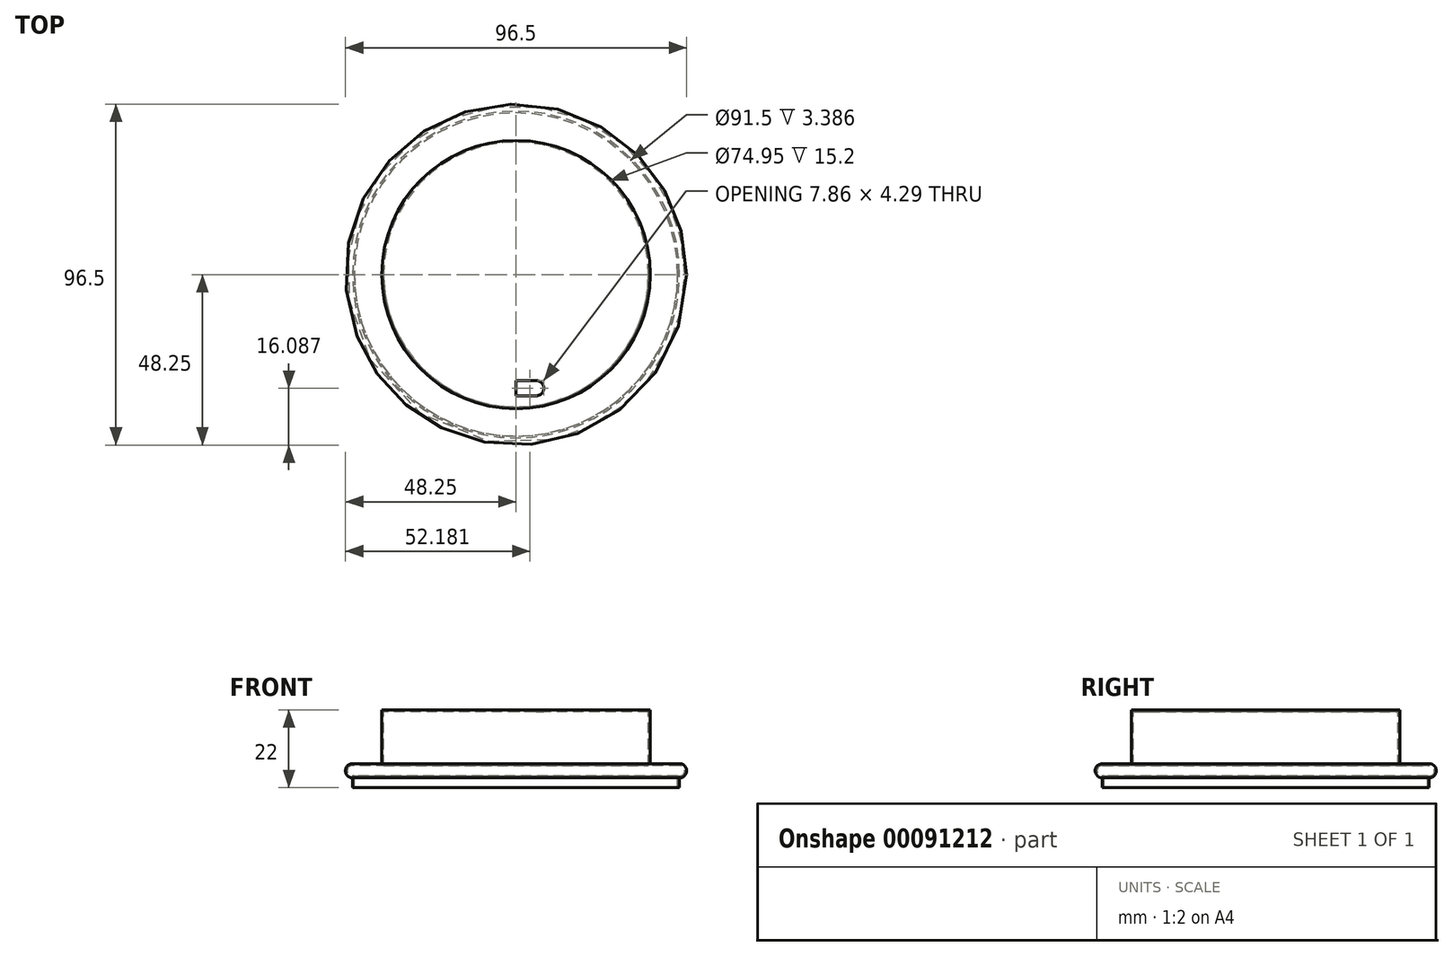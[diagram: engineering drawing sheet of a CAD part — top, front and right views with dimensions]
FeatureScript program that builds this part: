
annotation { "Feature Type Name" : "Feature", "Feature Type Description" : "" }
export const myFeature = defineFeature(function(context is Context, id is Id, definition is map)
    precondition{}
    {
        {
            var Q0;
            Q0=qCreatedBy(makeId("Front.planeOp"),FACE);
            var sketch = newSketch(context, id + "F0", { "sketchPlane" : qUnion([Q0])});
            skLineSegment(sketch, "E0.bottom", {"start": v(46.25, -3.4) * mm, "end": v(-46.25, -3.4) * mm});
            skLineSegment(sketch, "E0.top", {"start": v(46.25, 3.4) * mm, "end": v(-46.25, 3.4) * mm});
            skLineSegment(sketch, "E0.left", {"start": v(46.25, -3.4) * mm, "end": v(46.25, 3.4) * mm});
            skLineSegment(sketch, "E0.right", {"start": v(-46.25, -3.4) * mm, "end": v(-46.25, 3.4) * mm});
            skPoint(sketch, "E0.middle", {"position": v(0, 0) * mm});
            skLineSegment(sketch, "E1.bottom", {"start": v(-38.82, 12.6) * mm, "end": v(37.98, 12.6) * mm});
            skLineSegment(sketch, "E1.top", {"start": v(-38.82, 0) * mm, "end": v(37.98, 0) * mm});
            skLineSegment(sketch, "E1.left", {"start": v(-38.82, 12.6) * mm, "end": v(-38.82, 0) * mm});
            skLineSegment(sketch, "E1.right", {"start": v(37.98, 12.6) * mm, "end": v(37.98, 0) * mm});
            skLineSegment(sketch, "E2", {"start": v(0, 32.32) * mm, "end": v(0, -32.54) * mm});
            skLineSegment(sketch, "E3.bottom", {"start": v(-38.82, 18.6) * mm, "end": v(37.98, 18.6) * mm});
            skLineSegment(sketch, "E3.left", {"start": v(-38.82, 18.6) * mm, "end": v(-38.82, 12.6) * mm});
            skLineSegment(sketch, "E3.right", {"start": v(37.98, 18.6) * mm, "end": v(37.98, 12.6) * mm});
            skArc(sketch, "E4", {"start": v(46.25, -0.6) * mm, "mid": v(48.25, 1.4) * mm, "end": v(46.25, 3.4) * mm});
            skSolve(sketch);
        }
        {
            var Q0;
            {var subQ5=sQuery(id+"F0.wireOp",EDGE,"E3.right");Q0=makeQuery(id+"F0.imprint","IMPRINT",FACE,{"disambiguationData":[TD([[makeQuery(id+"F0.imprint","IMPRINT",EDGE,{"derivedFrom":subQ5}),-1.0]])]});}
            var Q1;
            {var subQ0=sQuery(id+"F0.wireOp",EDGE,"E1.right");var subQ1=sQuery(id+"F0.wireOp",EDGE,"E0.top");var subQ2=makeQuery(id+"F0.imprint","INTERSECT",VERTEX,{"derivedFrom":[subQ1,subQ0]});Q1=makeQuery(id+"F0.imprint","IMPRINT",FACE,{"disambiguationData":[TD([[makeQuery(id+"F0.imprint","IMPRINT",EDGE,{"disambiguationData":[TD([[subQ2,-1.0]])],"derivedFrom":subQ1}),-1.0]])]});}
            var Q2;
            {var subQ0=sQuery(id+"F0.wireOp",EDGE,"E1.right");var subQ1=sQuery(id+"F0.wireOp",EDGE,"E0.top");var subQ2=makeQuery(id+"F0.imprint","INTERSECT",VERTEX,{"derivedFrom":[subQ1,subQ0]});Q2=makeQuery(id+"F0.imprint","IMPRINT",FACE,{"disambiguationData":[TD([[makeQuery(id+"F0.imprint","IMPRINT",EDGE,{"disambiguationData":[TD([[subQ2,-1.0]])],"derivedFrom":subQ1}),1.0]])]});}
            var Q3;
            {var subQ5=sQuery(id+"F0.wireOp",EDGE,"E0.left");Q3=makeQuery(id+"F0.imprint","IMPRINT",FACE,{"disambiguationData":[TD([[makeQuery(id+"F0.imprint","IMPRINT",EDGE,{"derivedFrom":subQ5}),1.0]])]});}
            var Q4;
            {var subQ0=sQuery(id+"F0.wireOp",EDGE,"E4");Q4=makeQuery(id+"F0.imprint","IMPRINT",FACE,{"disambiguationData":[TD([[makeQuery(id+"F0.imprint","IMPRINT",EDGE,{"derivedFrom":subQ0}),1.0]])]});}
            var Q5;
            Q5=sQuery(id+"F0.wireOp",EDGE,"E2");
            revolve(context, id + "F1", {"entities" : qUnion([Q0, Q1, Q2, Q3, Q4]), "axis" : qUnion([Q5]), "revolveType" : RevolveType.FULL});
        }
        {
            var Q0;
            Q0=makeQuery(id+"F1.opRevolve","SWEPT_FACE",FACE,{"disambiguationData":[OSD([sQuery(id+"F0.wireOp",EDGE,"E3.bottom")])]});
            cPlane(context, id + "F2", {"entities" : qUnion([Q0]), "cplaneType" : CPlaneType.OFFSET, "offset" : 0 * mm, "width" : 150 * mm, "height" : 150 * mm});
        }
        {
            var Q0;
            Q0=makeQuery(id+"F1.opRevolve","SWEPT_FACE",FACE,{"disambiguationData":[OSD([sQuery(id+"F0.wireOp",EDGE,"E0.bottom")])]});
            shell(context, id + "F3", {"entities" : qUnion([Q0]), "thickness" : .5 * mm});
        }
        {
            var Q0;
            Q0=qCreatedBy(id+"F2.planeOp",FACE);
            var sketch = newSketch(context, id + "F4", { "sketchPlane" : qUnion([Q0])});
            skLineSegment(sketch, "E5", {"start": v(0, -55.1) * mm, "end": v(0, 54.97) * mm});
            skLineSegment(sketch, "E6", {"start": v(-6.37, -30.02) * mm, "end": v(5.72, -30.02) * mm});
            skLineSegment(sketch, "E7", {"start": v(5.72, -34.3) * mm, "end": v(-6.37, -34.3) * mm});
            skArc(sketch, "E8", {"start": v(5.72, -34.3) * mm, "mid": v(7.86, -32.16) * mm, "end": v(5.72, -30.02) * mm});
            skArc(sketch, "E9.MirrorCS", {"start": v(-5.72, -34.3) * mm, "mid": v(-7.86, -32.16) * mm, "end": v(-5.72, -30.02) * mm});
            skSolve(sketch);
        }
        {
            var Q0;
            {var subQ5=sQuery(id+"F4.wireOp",EDGE,"E8");Q0=makeQuery(id+"F4.imprint","IMPRINT",FACE,{"disambiguationData":[TD([[makeQuery(id+"F4.imprint","IMPRINT",EDGE,{"derivedFrom":subQ5}),1.0]])]});}
            var Q1;
            {var subQ5=sQuery(id+"F4.wireOp",EDGE,"E9.MirrorCS");Q1=makeQuery(id+"F4.imprint","IMPRINT",FACE,{"disambiguationData":[TD([[makeQuery(id+"F4.imprint","IMPRINT",EDGE,{"derivedFrom":subQ5}),-1.0]])]});}
            extrude(context, id + "F5", {"entities" : qUnion([Q0, Q1]), "operationType" : NewBodyOperationType.REMOVE, "oppositeDirection" : true, "depth" : 25 * mm});
        }
    });
